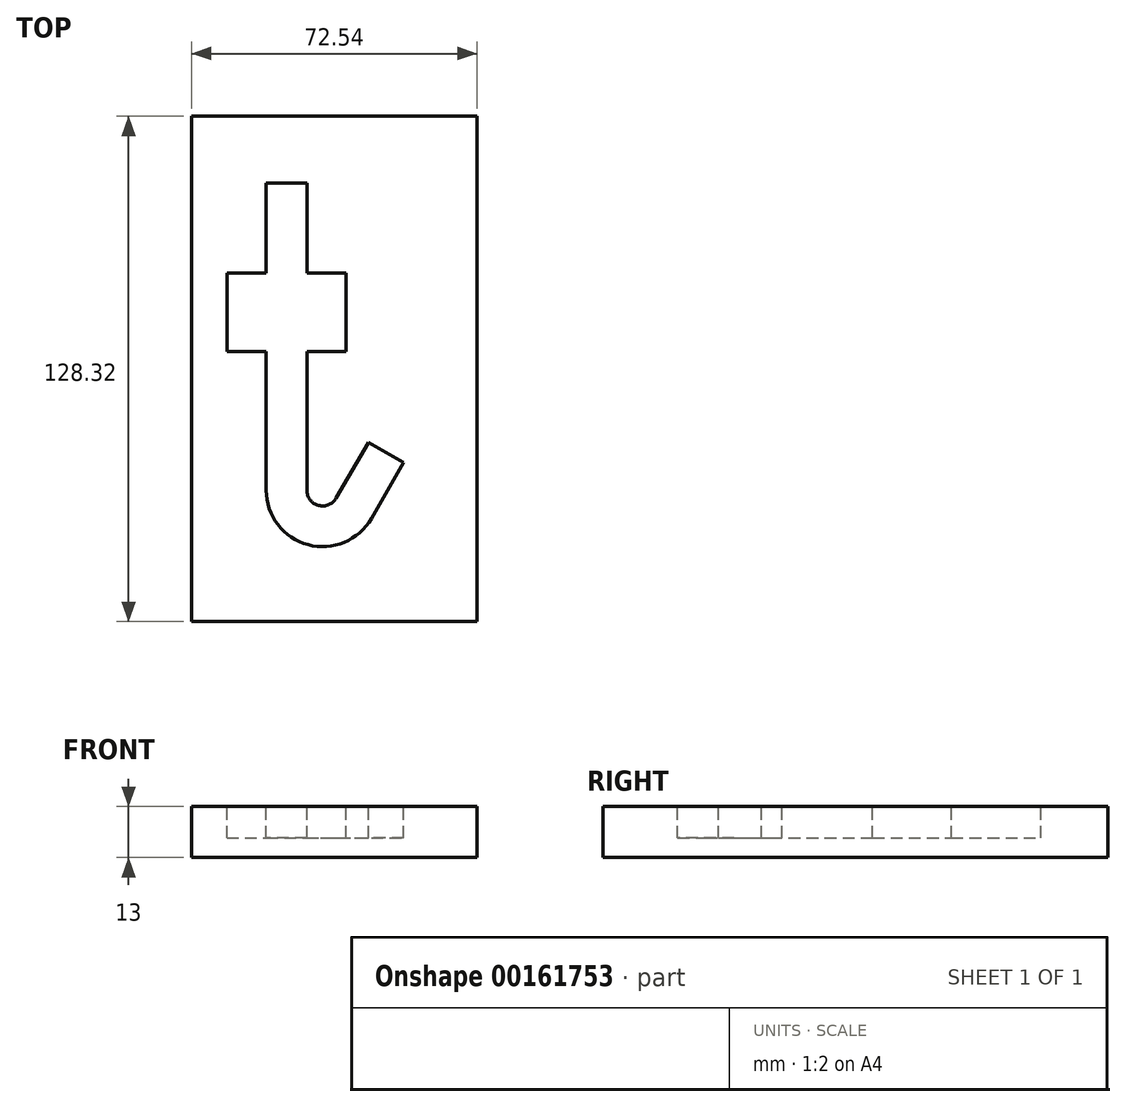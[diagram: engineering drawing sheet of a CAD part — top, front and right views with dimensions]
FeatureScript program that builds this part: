
annotation { "Feature Type Name" : "Feature", "Feature Type Description" : "" }
export const myFeature = defineFeature(function(context is Context, id is Id, definition is map)
    precondition{}
    {
        {
            var Q0;
            Q0=qCreatedBy(makeId("Top.planeOp"),FACE);
            var sketch = newSketch(context, id + "F0", { "sketchPlane" : qUnion([Q0])});
            skLineSegment(sketch, "E0", {"start": v(36.27, -64.16) * mm, "end": v(-36.27, -64.16) * mm});
            skLineSegment(sketch, "E1", {"start": v(36.27, 64.16) * mm, "end": v(-36.27, 64.16) * mm});
            skLineSegment(sketch, "E2", {"start": v(-36.27, -64.16) * mm, "end": v(-36.27, 64.16) * mm});
            skLineSegment(sketch, "E3", {"start": v(36.27, 64.16) * mm, "end": v(36.27, -64.16) * mm});
            skSolve(sketch);
        }
        {
            var Q0;
            Q0 = qSketchRegion(id + "F0", true);
            extrude(context, id + "F1", {"entities" : qUnion([Q0]), "depth" : 13 * mm});
        }
        {
            var Q0;
            Q0=makeQuery(id+"F1.opExtrude","CAP_FACE",FACE,{"disambiguationData":[OSD([sQuery(id+"F0.wireOp",EDGE,"E0"),sQuery(id+"F0.wireOp",EDGE,"E1"),sQuery(id+"F0.wireOp",EDGE,"E2"),sQuery(id+"F0.wireOp",EDGE,"E3")])],"isStart":false});
            var sketch = newSketch(context, id + "F2", { "sketchPlane" : qUnion([Q0])});
            skLineSegment(sketch, "E4", {"start": v(-6.94, 47.16) * mm, "end": v(-17.27, 47.16) * mm});
            skLineSegment(sketch, "E5", {"start": v(-6.94, -30.84) * mm, "end": v(-6.94, 4.36) * mm});
            skLineSegment(sketch, "E6", {"start": v(-17.27, -30.84) * mm, "end": v(-17.27, 4.36) * mm});
            skArc(sketch, "E7", {"start": v(-17.27, -30.84) * mm, "mid": v(-6.65, -44.68) * mm, "end": v(9.47, -38) * mm});
            skArc(sketch, "E8", {"start": v(-6.94, -30.83) * mm, "mid": v(-3.98, -34.7) * mm, "end": v(0.52, -32.83) * mm});
            skLineSegment(sketch, "E9", {"start": v(0.52, -32.83) * mm, "end": v(8.7, -18.68) * mm});
            skLineSegment(sketch, "E10", {"start": v(17.64, -23.85) * mm, "end": v(8.7, -18.68) * mm});
            skLineSegment(sketch, "E11", {"start": v(9.47, -38) * mm, "end": v(17.64, -23.85) * mm});
            skLineSegment(sketch, "E12", {"start": v(-27.27, 24.36) * mm, "end": v(-17.27, 24.36) * mm});
            skLineSegment(sketch, "E13", {"start": v(-27.27, 4.36) * mm, "end": v(-17.27, 4.36) * mm});
            skLineSegment(sketch, "E14", {"start": v(-27.27, 4.36) * mm, "end": v(-27.27, 24.36) * mm});
            skLineSegment(sketch, "E15", {"start": v(3.06, 4.36) * mm, "end": v(3.06, 24.36) * mm});
            skLineSegment(sketch, "E16", {"start": v(-6.94, 4.36) * mm, "end": v(3.06, 4.36) * mm});
            skLineSegment(sketch, "E17", {"start": v(-6.94, 24.36) * mm, "end": v(3.06, 24.36) * mm});
            skLineSegment(sketch, "E18", {"start": v(-17.27, 24.36) * mm, "end": v(-17.27, 47.16) * mm});
            skLineSegment(sketch, "E19", {"start": v(-6.94, 24.36) * mm, "end": v(-6.94, 47.16) * mm});
            skLineSegment(sketch, "E20", {"start": v(-17.27, 47.16) * mm, "end": v(-6.94, 47.16) * mm});
            skLineSegment(sketch, "E21", {"start": v(3.06, 4.36) * mm, "end": v(-6.94, 4.36) * mm});
            skFitSpline(sketch, "E22", {"points": [v(0.52, -32.83) * mm, v(8.7, -18.68) * mm], "startDerivative": vector(8.17, 14.15) * mm, "endDerivative": vector(8.17, 14.15) * mm});
            skLineSegment(sketch, "E23", {"start": v(17.64, -23.85) * mm, "end": v(9.47, -38) * mm});
            skArc(sketch, "E24", {"start": v(-17.27, -30.83) * mm, "mid": v(-6.65, -44.68) * mm, "end": v(9.47, -38) * mm});
            skSolve(sketch);
        }
        {
            var Q0;
            {var subQ0=sQuery(id+"F2.wireOp",EDGE,"E5");Q0=makeQuery(id+"F2.imprint","IMPRINT",FACE,{"disambiguationData":[TD([[makeQuery(id+"F2.imprint","IMPRINT",EDGE,{"derivedFrom":subQ0}),1.0]])]});}
            extrude(context, id + "F3", {"entities" : qUnion([Q0]), "operationType" : NewBodyOperationType.REMOVE, "oppositeDirection" : true, "depth" : 8 * mm});
        }
    });
